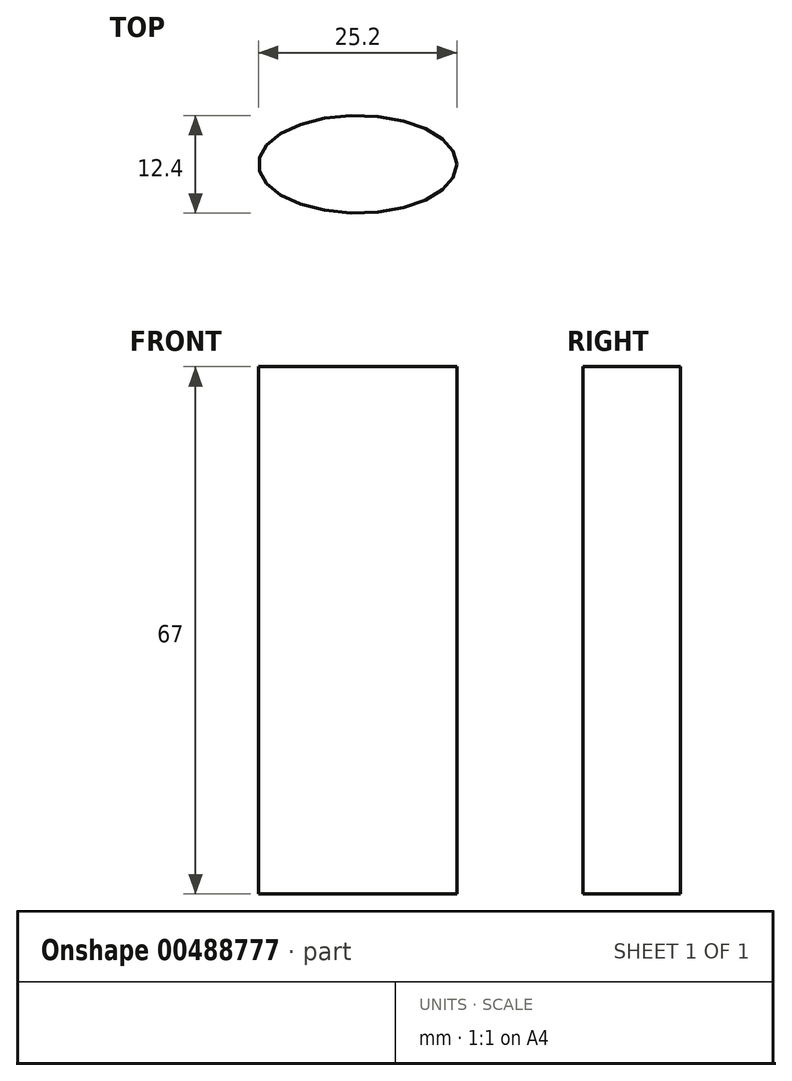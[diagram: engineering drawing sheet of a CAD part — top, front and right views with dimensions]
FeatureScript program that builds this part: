
annotation { "Feature Type Name" : "Feature", "Feature Type Description" : "" }
export const myFeature = defineFeature(function(context is Context, id is Id, definition is map)
    precondition{}
    {
        {
            var Q0;
            Q0=qCreatedBy(makeId("Top.planeOp"),FACE);
            var sketch = newSketch(context, id + "F0", { "sketchPlane" : qUnion([Q0])});
            skEllipse(sketch, "E0", {"center": v(0, 0) * mm, "majorRadius": 12.6 * mm, "minorRadius": 6.2 * mm, "majorAxis": v(1, 0)});
            skFitSpline(sketch, "E1.0", {"points": [v(11.5, -0.82) * mm, v(11.65, 0) * mm, v(11.5, 0.82) * mm, v(11.04, 1.57) * mm, v(10.45, 2.19) * mm, v(9.71, 2.8) * mm, v(8.53, 3.5) * mm, v(7.04, 4.11) * mm, v(5.7, 4.5) * mm, v(4.27, 4.84) * mm, v(2.76, 5.07) * mm, v(1.2, 5.18) * mm, v(0, 5.2) * mm, v(-1.2, 5.18) * mm, v(-2.76, 5.07) * mm, v(-4.27, 4.84) * mm, v(-5.7, 4.5) * mm, v(-7.04, 4.11) * mm, v(-8.53, 3.5) * mm, v(-9.71, 2.8) * mm, v(-10.45, 2.19) * mm, v(-11.04, 1.57) * mm, v(-11.5, 0.82) * mm, v(-11.65, 0) * mm, v(-11.5, -0.82) * mm, v(-11.04, -1.57) * mm, v(-10.45, -2.19) * mm, v(-9.71, -2.8) * mm, v(-8.53, -3.5) * mm, v(-7.04, -4.11) * mm, v(-5.7, -4.5) * mm, v(-4.27, -4.84) * mm, v(-2.76, -5.07) * mm, v(-1.2, -5.18) * mm, v(0, -5.2) * mm, v(1.2, -5.18) * mm, v(2.76, -5.07) * mm, v(4.27, -4.84) * mm, v(5.7, -4.5) * mm, v(7.04, -4.11) * mm, v(8.53, -3.5) * mm, v(9.71, -2.8) * mm, v(10.45, -2.19) * mm, v(11.04, -1.57) * mm, v(11.5, -0.82) * mm, v(11.65, 0) * mm, v(11.5, 0.82) * mm, v(11.5, -0.82) * mm]});
            skSolve(sketch);
        }
        {
            var Q0;
            Q0=makeQuery(id+"F0.imprint","IMPRINT",FACE,{"disambiguationData":[TD([[makeQuery(id+"F0.imprint","IMPRINT",EDGE,{"derivedFrom":sQuery(id+"F0.wireOp",EDGE,"E0")}),1.0]])]});
            extrude(context, id + "F1", {"entities" : qUnion([Q0]), "depth" : 65 * mm});
        }
        {
            var Q0;
            Q0=makeQuery(id+"F1.opExtrude","CAP_FACE",FACE,{"disambiguationData":[OSD([sQuery(id+"F0.wireOp",EDGE,"E0"),sQuery(id+"F0.wireOp",EDGE,"E1.0")])],"isStart":true});
            var Q1;
            Q1 = qSketchRegion(id + "F0", true);
            var Q2;
            Q2=makeQuery(id+"F0.imprint","IMPRINT",FACE,{"disambiguationData":[TD([[makeQuery(id+"F0.imprint","IMPRINT",EDGE,{"derivedFrom":sQuery(id+"F0.wireOp",EDGE,"E1.0")}),1.0]])]});
            extrude(context, id + "F2", {"entities" : qUnion([Q0, Q1, Q2]), "operationType" : NewBodyOperationType.ADD, "depth" : 2 * mm});
        }
    });
